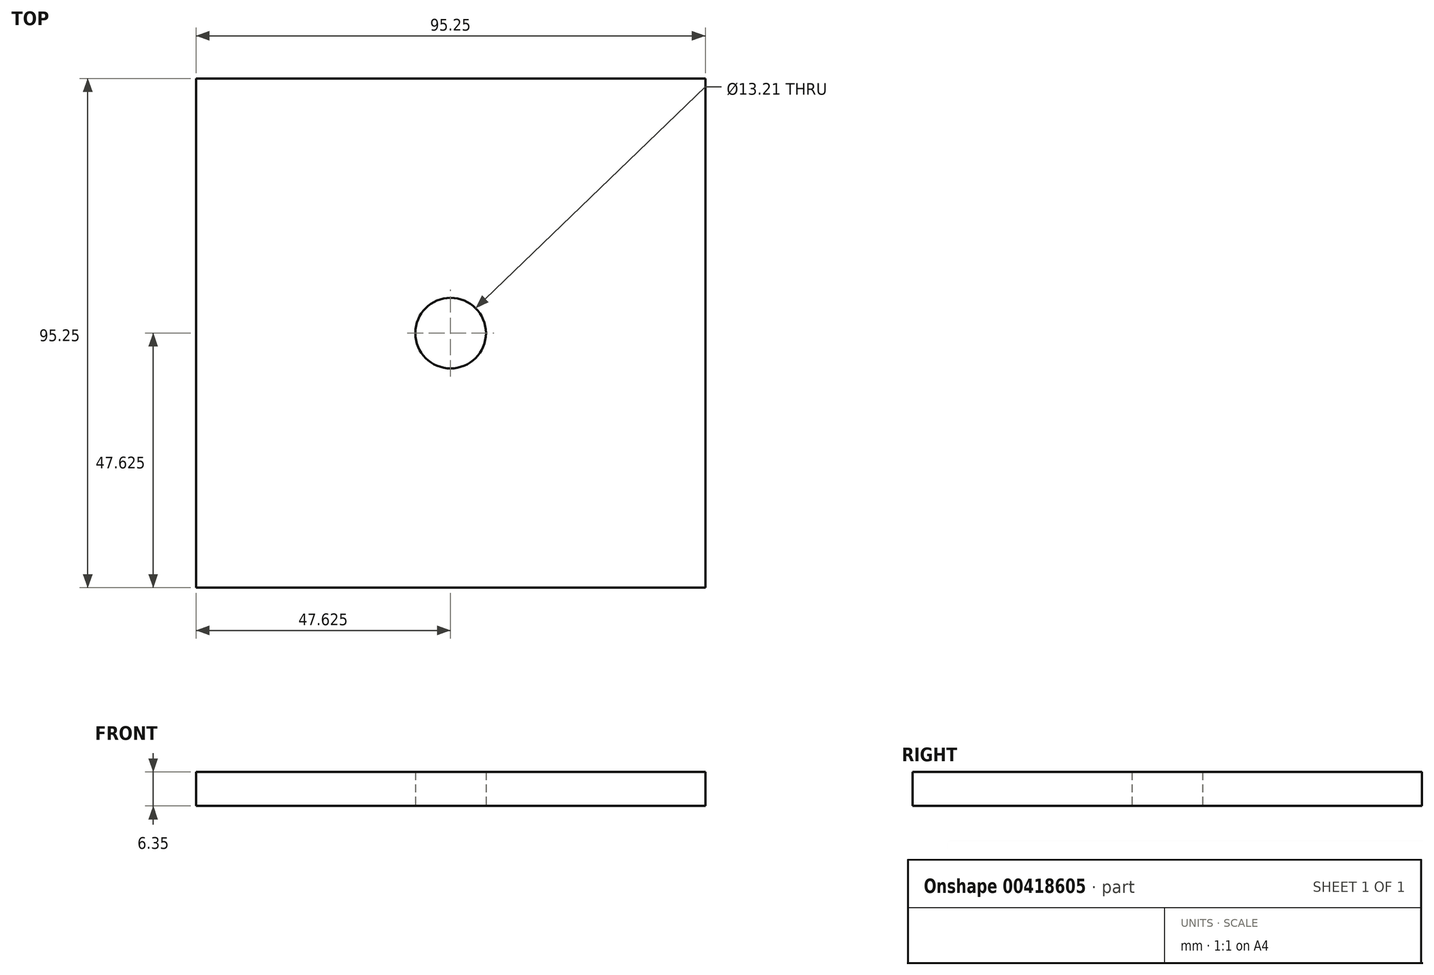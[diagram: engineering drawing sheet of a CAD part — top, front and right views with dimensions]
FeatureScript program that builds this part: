
annotation { "Feature Type Name" : "Feature", "Feature Type Description" : "" }
export const myFeature = defineFeature(function(context is Context, id is Id, definition is map)
    precondition{}
    {
        {
            var Q0;
            Q0=qCreatedBy(makeId("Top.planeOp"),FACE);
            var sketch = newSketch(context, id + "F0", { "sketchPlane" : qUnion([Q0])});
            skLineSegment(sketch, "E0.bottom", {"start": v(0, 0) * mm, "end": v(-95.25, 0) * mm});
            skLineSegment(sketch, "E0.top", {"start": v(0, -95.25) * mm, "end": v(-95.25, -95.25) * mm});
            skLineSegment(sketch, "E0.left", {"start": v(0, 0) * mm, "end": v(0, -95.25) * mm});
            skLineSegment(sketch, "E0.right", {"start": v(-95.25, 0) * mm, "end": v(-95.25, -95.25) * mm});
            skPoint(sketch, "E1", {"position": v(-47.63, -47.63) * mm});
            skPoint(sketch, "E1.positionSnap0", {"position": v(-47.63, 0) * mm});
            skPoint(sketch, "E1.positionSnap1", {"position": v(0, -47.63) * mm});
            skCircle(sketch, "E2", {"center": v(-47.63, -47.63) * mm, "radius": 6.6 * mm});
            skSolve(sketch);
        }
        {
            var Q0;
            Q0=makeQuery(id+"F0.imprint","IMPRINT",FACE,{"disambiguationData":[TD([[makeQuery(id+"F0.imprint","IMPRINT",EDGE,{"derivedFrom":sQuery(id+"F0.wireOp",EDGE,"E0.bottom")}),1.0]])]});
            extrude(context, id + "F1", {"entities" : qUnion([Q0]), "depth" : 6.35 * mm});
        }
    });
